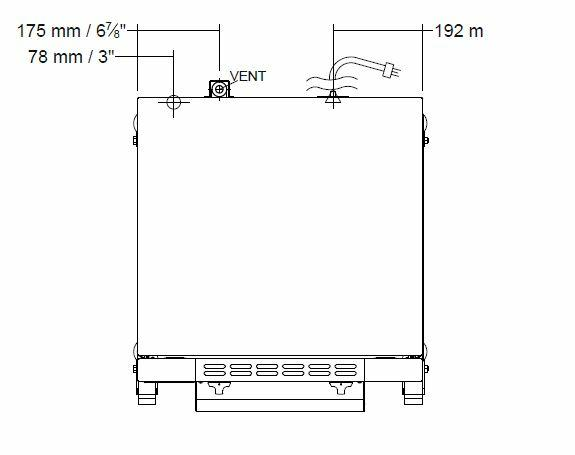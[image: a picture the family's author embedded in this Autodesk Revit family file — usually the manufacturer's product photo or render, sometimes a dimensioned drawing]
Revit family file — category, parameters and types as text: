
# Revit family: QF_MOFFAT_E27D3-2C_NZ
name_source: partatom
category: Specialty Equipment
revit_build: Autodesk Revit 2014 (Build: 20130308_1515(x64)
units: mm (PartAtom-declared; Revit-internal decimal feet)

## types (1)
- QF_MOFFAT_E27D3-2C_NZ
    Apparent Power = 4508 VA
    Cold Water Connection Height = 0 mm  [stored 0 ft]
    Cold Water Flow = 0 GPM
    Cold Water Maximum Pressure = 80.00 psi
    Cold Water Minimum Pressure = 20.00 psi
    Cold Water RI Height = 0 mm  [stored 0 ft]
    Cold Water Size = 1"
    Cold Water Temperature Recommended = 0 °F
    Conn Conduit = Yes
    Cycle = 50 Hz
    Depth = 762 mm  [stored 2.5 ft]
    Description = FULL SIZE DIGITAL / ELECTRIC CONVECTION OVENS DOUBLE STACKED ON A STAINLESS STEEL BASE STAND
    Elec Conn Connection Height = 0 mm  [stored 0 ft]
    Elec Conn RI Height = 0 mm  [stored 0 ft]
    Electrical Remarks = 230-240V, 50Hz, 1P+N+E, 4.7kW, 19.6A
    Exhaust RI Height = 0 mm  [stored 0 ft]
    Exhaust Static Press = 0.00 in-wg
    Exhaust Vent Depth = 0 mm  [stored 0 ft]
    Exhaust Vent Diameter = 0 mm  [stored 0 ft]
    Exhaust Vent Width = 0 mm  [stored 0 ft]
    Exhaust Volume = 0 CFM
    FL Amps = 20 A
    Foodservice Equipment Identifier = Yes
    Height = 1653 mm  [stored 5.42323 ft]
    Height of Stand = 536 mm  [stored 1.75853 ft]
    Identify Quantity as Lot = Yes
    Length = 810 mm  [stored 2.65748 ft]
    Manufacturer = MOFFAT
    Max Overcurrent Protection = 0 A
    Min Ckt Ampacity = 0 A
    Model = E27D3-2C
    Number of Poles = 1
    Phase = 1
    URL = www.moffat.com.au
    URL Cutsheet = www.moffat.com.au
    Volts = 230 V
    Watts = 4700 W
    Weight in Pounds = 0

note: [stored X ft] marks values corroborated as IEEE doubles in the binary element streams (Revit-internal decimal feet)

## geometry (parser evidence)
native form markers: Blend x16, Sweep x9
no freeform markers — native parametric forms only
